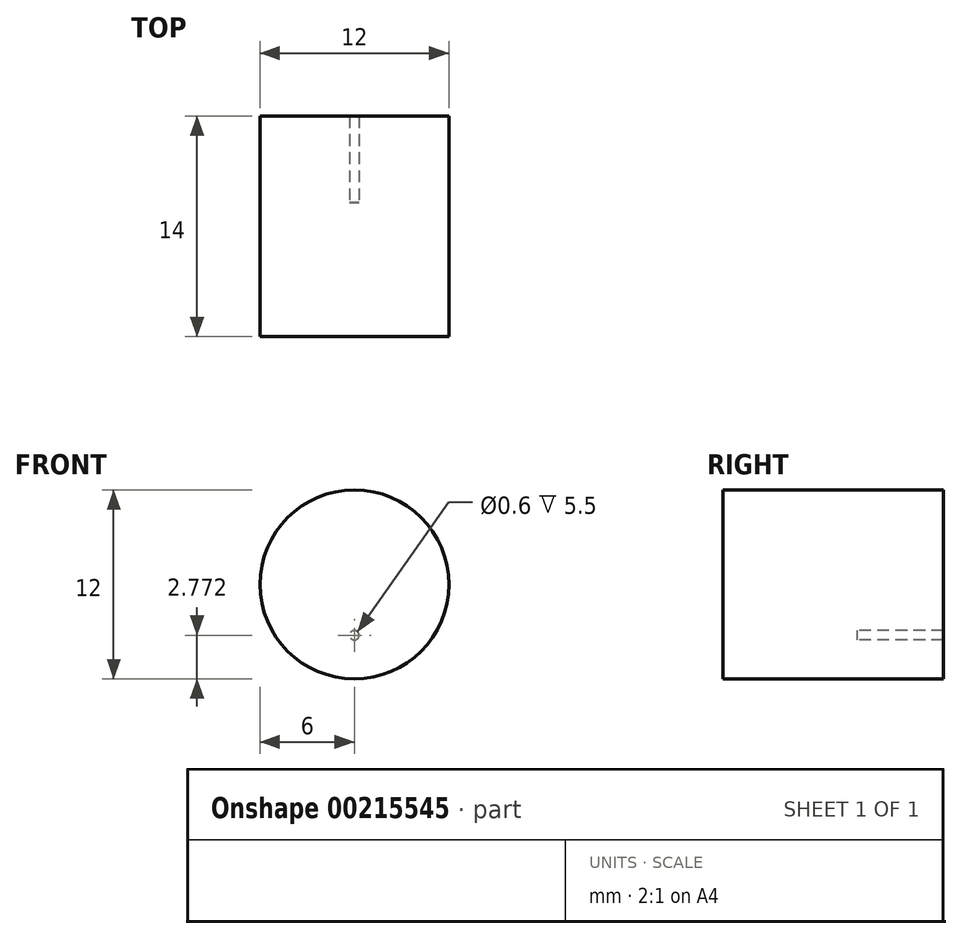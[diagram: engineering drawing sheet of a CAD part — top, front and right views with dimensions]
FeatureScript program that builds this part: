
annotation { "Feature Type Name" : "Feature", "Feature Type Description" : "" }
export const myFeature = defineFeature(function(context is Context, id is Id, definition is map)
    precondition{}
    {
        {
            var Q0;
            Q0=qCreatedBy(makeId("Front.planeOp"),FACE);
            var sketch = newSketch(context, id + "F0", { "sketchPlane" : qUnion([Q0])});
            skCircle(sketch, "E0", {"center": v(0, 0) * mm, "radius": 6 * mm});
            skSolve(sketch);
        }
        {
            var Q0;
            Q0 = qSketchRegion(id + "F0", true);
            extrude(context, id + "F1", {"entities" : qUnion([Q0]), "depth" : 8.5 * mm});
        }
        {
            var Q0;
            Q0=makeQuery(id+"F1.opExtrude","CAP_FACE",FACE,{"disambiguationData":[OSD([sQuery(id+"F0.wireOp",EDGE,"E0")])],"isStart":true});
            var sketch = newSketch(context, id + "F2", { "sketchPlane" : qUnion([Q0])});
            skCircle(sketch, "E1", {"center": v(0, 3.23) * mm, "radius": 0.3 * mm});
            skCircle(sketch, "E2.MirrorC", {"center": v(0, -3.23) * mm, "radius": 0.3 * mm});
            skSolve(sketch);
        }
        {
            var Q0;
            Q0=makeQuery(id+"F2.imprint","IMPRINT",FACE,{"disambiguationData":[TD([[makeQuery(id+"F2.imprint","IMPRINT",EDGE,{"derivedFrom":sQuery(id+"F2.wireOp",EDGE,"E1")}),1.0]])]});
            var Q1;
            Q1=makeQuery(id+"F2.imprint","IMPRINT",FACE,{"disambiguationData":[TD([[makeQuery(id+"F2.imprint","IMPRINT",EDGE,{"derivedFrom":sQuery(id+"F2.wireOp",EDGE,"E2.MirrorC")}),-1.0]])]});
            extrude(context, id + "F3", {"entities" : qUnion([Q0, Q1]), "operationType" : NewBodyOperationType.ADD, "depth" : 5.5 * mm});
        }
    });
